# Revit family: P190780JX-232c_JFFCC72EFS_StainlessSteel_JA_Refrigeraton_FS_FDBM
name_source: partatom
category: Specialty Equipment
units: mm (PartAtom-declared; Revit-internal decimal feet)

## family parameters
Always vertical = Yes
Cut with Voids When Loaded = No
Enable Cutting in Views = No
Maintain Annotation Orientation = No
Part Type = Normal
Room Calculation Point = No
Round Connector Dimension = Use Diameter
Shared = No
Work Plane-Based = No

## types (1)
- JFFCC72EFS
    Accent Material = ARCAT - Metal - Steel - Black
    Amps = 0 A
    Body Material = ARCAT - Metal - Steel - Stainless
    Clearance Material = ARCAT - Clearance
    Default Elevation = 0"
    Depth = 31 1/4"
    Description = Euro-Style 72” Counter-Depth French Door Refrigerator with Obsidian Interior
Réfrigérateur à portes françaises Jenn-Air® à profondeur de comptoir et intérieur obsidienne, 72 po
    Dimension Guide = http://access.whirlpool.com Guide&sku=JFFCC72EFS&language=EN
http://access.whirlpool.com Guide&sku=JFFCC72EFS&language=EN
    Door Material = ARCAT - Metal - Steel - Stainless
    Energy Guide = http://access.whirlpool.com Guide&sku=JFFCC72EFS&language=EN
http://access.whirlpool.com Guide&sku=JFFCC72EFS&language=FR
    Family Name = FS FDBM Euro
    Feature 1 = Obsidian Interior
Intérieur noir obsidienne
    Feature 2 = WiFi Connectivity
Connectivité WiFi
    Feature 3 = Twin Fresh™ Climate Control System
Système de contrôle de température Twin Fresh™
    Handle Material = ARCAT - Metal - Steel - Stainless
    Height = 71 15/16"
    Manufacturer = Jenn Air
    Model = JFFCC72EFS
    Voltage = 0 V
    Wheel Material = ARCAT - Plastic - Black
    Width = 35 3/4"

## geometry (parser evidence)
native form markers: Sweep x3
no freeform markers — native parametric forms only
